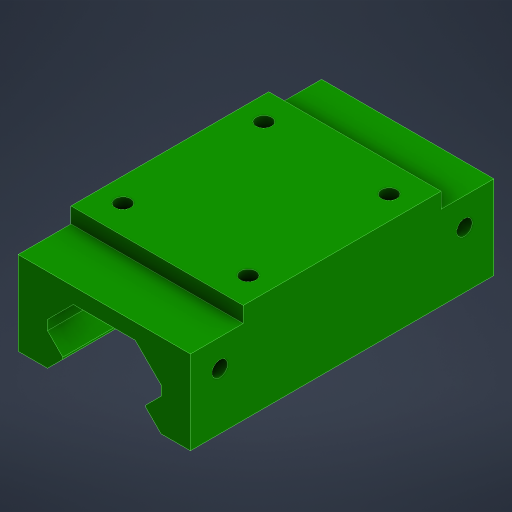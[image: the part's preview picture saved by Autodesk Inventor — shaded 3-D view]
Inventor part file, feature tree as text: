
AUTODESK INVENTOR PART (.ipt)
format: ipt  version: 2024.2 (Build 282272000, 272)  size: 264,704 bytes
history: native  units: mm
features: extrude x4, sketch x3, mirror x1
ambient origin geometry x8: Origin, YZ Plane, XZ Plane, XY Plane, X Axis, Y Axis, Z Axis, Center Point
bodies: Solid1 (feature_tree)
feature tree (8):
  extrude  "Extrusion1"  Depth=44.0mm
  sketch  "Sketch2"  dims[d3=17.5mm d4=20.0mm d5=4.6mm d6=8.5mm d7=135.0deg d8=0.5mm d9=135.0deg d10=2.5mm d11=7.5mm d12=25.4mm]
  extrude  "Extrusion2"  Depth=25.4mm
  extrude  "Extrusion3"  TaperAngle=135.0deg  [1 undecoded]
  extrude  "Extrusion4"  Depth=2.5mm
  mirror  "Mirror1"
  sketch  "Sketch1"  dims[d0=4.6mm d1=44.0mm]
  sketch  "Sketch3"  dims[d13=45.0deg d14=135.0deg d15=2.5mm d16=0.5mm d17=135.0deg d19=4.5mm d20=77.5mm d21=0.0mm d22=36.0mm d23=4.0mm d24=4.0mm d25=36.0mm d26=4.0mm d27=4.0mm d29=32.0mm d30=50.5mm d31=8.0mm d32=0.0mm d33=4.0mm d34=0.0mm d35=6.0mm d36=6.0mm d37=7.0mm d38=7.0mm d39=4.0mm d40=4.0mm d41=5.0mm d42=0.0mm]
note: 1 required parameter value undecoded (feature->parameter linkage not recoverable at this tier; creation-order binding heuristic only, values carry confidence <= 0.55)
